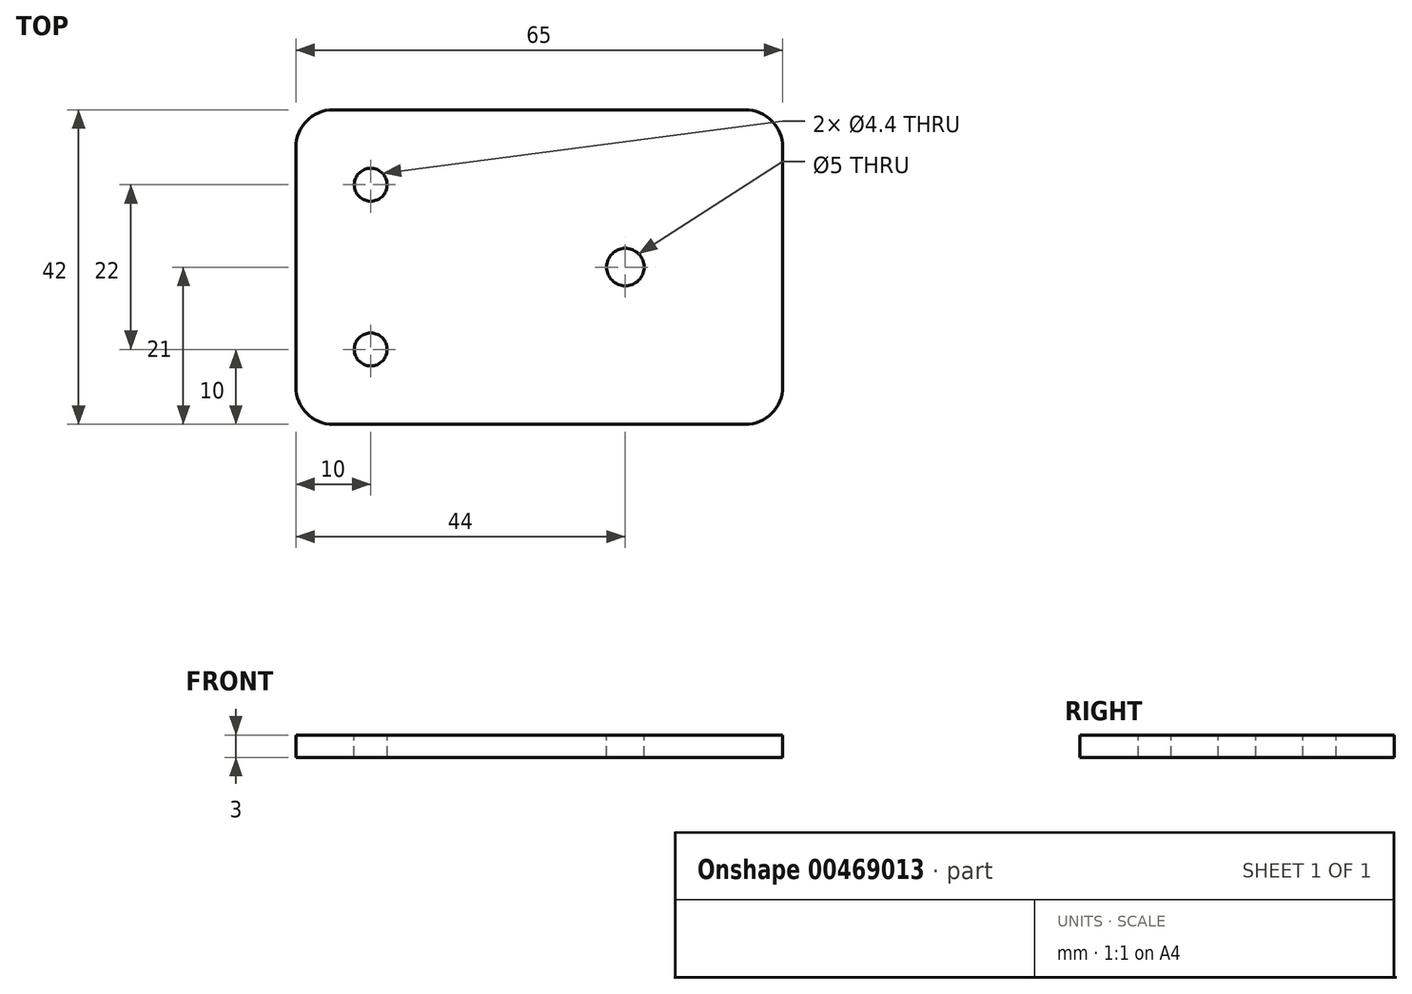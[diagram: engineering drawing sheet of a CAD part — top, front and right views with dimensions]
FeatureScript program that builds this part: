
annotation { "Feature Type Name" : "Feature", "Feature Type Description" : "" }
export const myFeature = defineFeature(function(context is Context, id is Id, definition is map)
    precondition{}
    {
        {
            var Q0;
            Q0=qCreatedBy(makeId("Top.planeOp"),FACE);
            var sketch = newSketch(context, id + "F0", { "sketchPlane" : qUnion([Q0])});
            skLineSegment(sketch, "E0.bottom", {"start": v(0, 0) * mm, "end": v(65, 0) * mm});
            skLineSegment(sketch, "E0.top", {"start": v(0, -42) * mm, "end": v(65, -42) * mm});
            skLineSegment(sketch, "E0.left", {"start": v(0, 0) * mm, "end": v(0, -42) * mm});
            skLineSegment(sketch, "E0.right", {"start": v(65, 0) * mm, "end": v(65, -42) * mm});
            skSolve(sketch);
        }
        {
            var Q0;
            Q0=makeQuery(id+"F0.imprint","IMPRINT",FACE,{"disambiguationData":[TD([[makeQuery(id+"F0.imprint","IMPRINT",EDGE,{"derivedFrom":sQuery(id+"F0.wireOp",EDGE,"E0.bottom")}),-1.0]])]});
            extrude(context, id + "F1", {"entities" : qUnion([Q0]), "depth" : 3 * mm});
        }
        {
            var Q0;
            Q0=makeQuery(id+"F1.opExtrude","CAP_FACE",FACE,{"disambiguationData":[OSD([sQuery(id+"F0.wireOp",EDGE,"E0.bottom"),sQuery(id+"F0.wireOp",EDGE,"E0.top"),sQuery(id+"F0.wireOp",EDGE,"E0.left"),sQuery(id+"F0.wireOp",EDGE,"E0.right")])],"isStart":false});
            var sketch = newSketch(context, id + "F2", { "sketchPlane" : qUnion([Q0])});
            skLineSegment(sketch, "E1", {"start": v(65, -21) * mm, "end": v(44, -21) * mm, "construction": true});
            skLineSegment(sketch, "E2", {"start": v(44, -21) * mm, "end": v(44, 0) * mm, "construction": true});
            skLineSegment(sketch, "E3", {"start": v(10, 0) * mm, "end": v(10, -42) * mm, "construction": true});
            skPoint(sketch, "E4", {"position": v(10, -10) * mm});
            skPoint(sketch, "E5.MirrorP", {"position": v(10, -32) * mm});
            skLineSegment(sketch, "E6.bottom", {"start": v(59.5, -5.5) * mm, "end": v(28.5, -5.5) * mm, "construction": true});
            skLineSegment(sketch, "E6.top", {"start": v(59.5, -36.5) * mm, "end": v(28.5, -36.5) * mm, "construction": true});
            skLineSegment(sketch, "E6.left", {"start": v(59.5, -5.5) * mm, "end": v(59.5, -36.5) * mm, "construction": true});
            skLineSegment(sketch, "E6.right", {"start": v(28.5, -5.5) * mm, "end": v(28.5, -36.5) * mm, "construction": true});
            skPoint(sketch, "E6.middle", {"position": v(44, -21) * mm});
            skSolve(sketch);
        }
        {
            var Q0;
            Q0=sQuery(id+"F2.wireOp",VERTEX,"E4");
            var Q1;
            Q1=sQuery(id+"F2.wireOp",VERTEX,"E5.MirrorP");
            var Q2;
            Q2=makeQuery(id+"F1.opExtrude","SWEPT_BODY",BODY,{"disambiguationData":[OSD([sQuery(id+"F0.wireOp",EDGE,"E0.bottom"),sQuery(id+"F0.wireOp",EDGE,"E0.top"),sQuery(id+"F0.wireOp",EDGE,"E0.left"),sQuery(id+"F0.wireOp",EDGE,"E0.right")])]});
            hole(context, id + "F3", {"style" : HoleStyle.SIMPLE, "endStyle" : HoleEndStyle.THROUGH, "standardTappedOrClearance" : lookupTablePath({ "standard" : "ISO", "fit" : "Normal", "size" : "M4", "type" : "Clearance" }), "standardBlindInLast" : lookupTablePath({ "fit" : "Standard", "standard" : "ISO", "size" : "M4", "type" : "Clearance" }), "holeDiameter" : 4.4 * mm, "isTappedThrough" : true, "tappedDepth" : 12 * mm, "tapClearance" : 3, "locations" : qUnion([Q0, Q1]), "scope" : qUnion([Q2])});
        }
        {
            var Q0;
            Q0=sQuery(id+"F2.wireOp",VERTEX,"E6.middle");
            var Q1;
            Q1=makeQuery(id+"F1.opExtrude","SWEPT_BODY",BODY,{"disambiguationData":[OSD([sQuery(id+"F0.wireOp",EDGE,"E0.bottom"),sQuery(id+"F0.wireOp",EDGE,"E0.top"),sQuery(id+"F0.wireOp",EDGE,"E0.left"),sQuery(id+"F0.wireOp",EDGE,"E0.right")])]});
            hole(context, id + "F4", {"style" : HoleStyle.SIMPLE, "endStyle" : HoleEndStyle.THROUGH, "holeDiameter" : 5 * mm, "isTappedThrough" : true, "tappedDepth" : 12 * mm, "tapClearance" : 3, "locations" : qUnion([Q0]), "scope" : qUnion([Q1])});
        }
        {
            var Q0;
            Q0=makeQuery(id+"F1.opExtrude","SWEPT_EDGE",EDGE,{"disambiguationData":[OSD([sQuery(id+"F0.wireOp",EDGE,"E0.top"),sQuery(id+"F0.wireOp",EDGE,"E0.left")])]});
            var Q1;
            Q1=makeQuery(id+"F1.opExtrude","SWEPT_EDGE",EDGE,{"disambiguationData":[OSD([sQuery(id+"F0.wireOp",EDGE,"E0.top"),sQuery(id+"F0.wireOp",EDGE,"E0.right")])]});
            var Q2;
            Q2=makeQuery(id+"F1.opExtrude","SWEPT_EDGE",EDGE,{"disambiguationData":[OSD([sQuery(id+"F0.wireOp",EDGE,"E0.bottom"),sQuery(id+"F0.wireOp",EDGE,"E0.right")])]});
            var Q3;
            Q3=makeQuery(id+"F1.opExtrude","SWEPT_EDGE",EDGE,{"disambiguationData":[OSD([sQuery(id+"F0.wireOp",EDGE,"E0.bottom"),sQuery(id+"F0.wireOp",EDGE,"E0.left")])]});
            fillet(context, id + "F5", {"entities" : qUnion([Q0, Q1, Q2, Q3]), "radius" : 5 * mm, "tangentPropagation" : true, "allowEdgeOverflow" : false});
        }
    });
